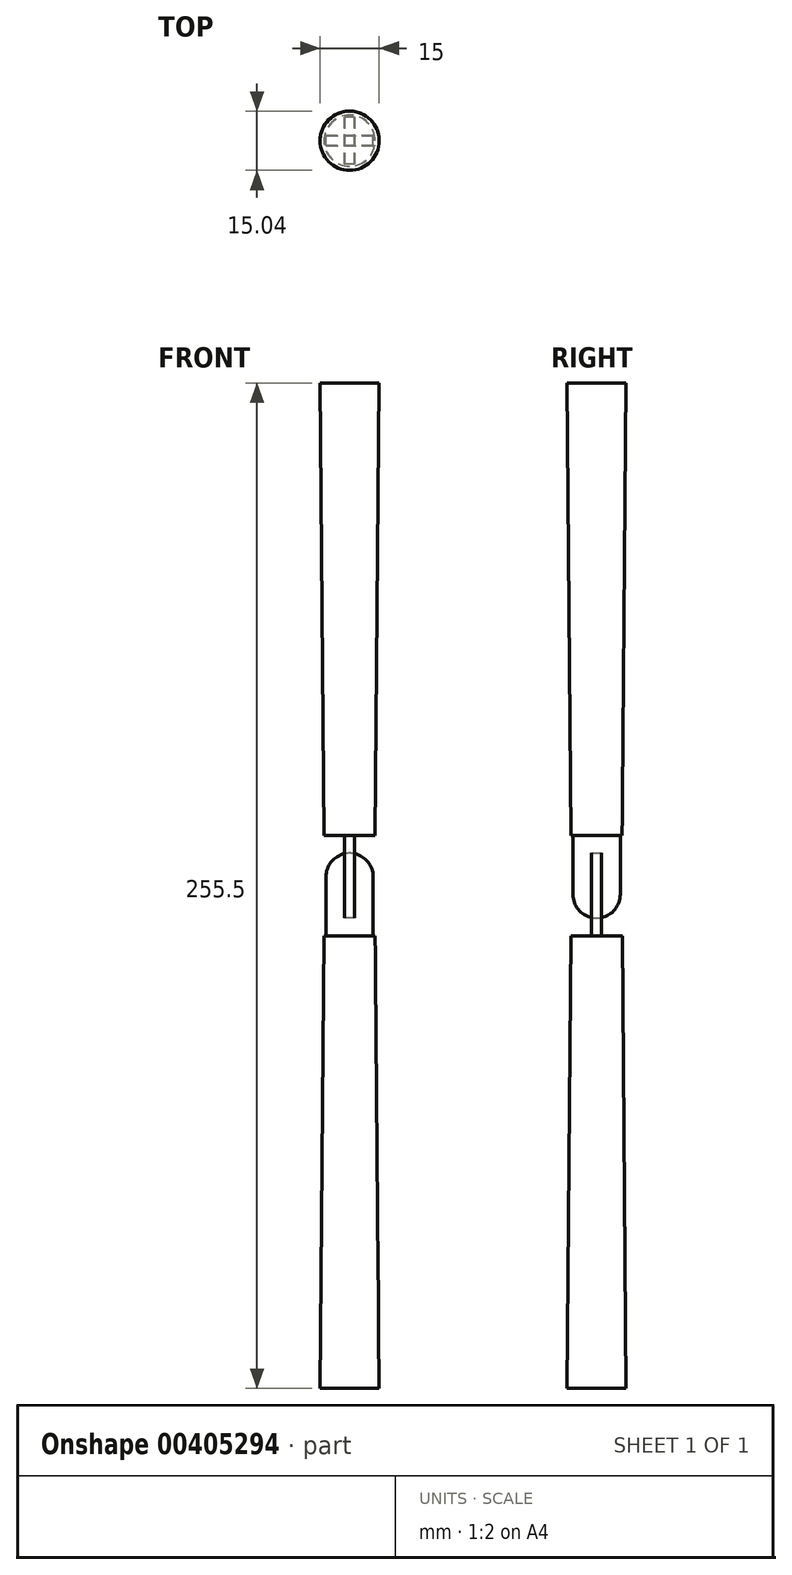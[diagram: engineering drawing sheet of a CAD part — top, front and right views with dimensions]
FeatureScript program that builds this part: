
annotation { "Feature Type Name" : "Feature", "Feature Type Description" : "" }
export const myFeature = defineFeature(function(context is Context, id is Id, definition is map)
    precondition{}
    {
        {
            var Q0;
            Q0=qCreatedBy(makeId("Front.planeOp"),FACE);
            var sketch = newSketch(context, id + "F0", { "sketchPlane" : qUnion([Q0])});
            skLineSegment(sketch, "E0.top", {"start": v(-6, 0) * mm, "end": v(6, 0) * mm});
            skLineSegment(sketch, "E0.left", {"start": v(-6, 15) * mm, "end": v(-6, 0) * mm});
            skArc(sketch, "E1", {"start": v(6, 15) * mm, "mid": v(0, 21) * mm, "end": v(-6, 15) * mm});
            skArc(sketch, "E2", {"start": v(3, 15) * mm, "mid": v(-2.12, 17.12) * mm, "end": v(0, 12) * mm});
            skCircle(sketch, "E3", {"center": v(0, 6) * mm, "radius": 2 * mm});
            skArc(sketch, "E4", {"start": v(6, 6) * mm, "mid": v(4.24, 10.24) * mm, "end": v(0, 12) * mm});
            skLineSegment(sketch, "E5", {"start": v(6, 0) * mm, "end": v(6, 6) * mm});
            skArc(sketch, "E6", {"start": v(3, 15) * mm, "mid": v(4.5, 13.5) * mm, "end": v(6, 15) * mm});
            skPoint(sketch, "E7.start.orphan", {"position": v(3, 15) * mm});
            skSolve(sketch);
        }
        {
            var Q0;
            Q0=makeQuery(id+"F0.imprint","IMPRINT",FACE,{"disambiguationData":[TD([[makeQuery(id+"F0.imprint","IMPRINT",EDGE,{"derivedFrom":sQuery(id+"F0.wireOp",EDGE,"E0.top")}),1.0]])]});
            extrude(context, id + "F1", {"entities" : qUnion([Q0]), "endBound" : BoundingType.SYMMETRIC, "depth" : 2.5 * mm});
        }
        {
            var Q0;
            Q0=qCreatedBy(makeId("Right.planeOp"),FACE);
            var sketch = newSketch(context, id + "F2", { "sketchPlane" : qUnion([Q0])});
            skLineSegment(sketch, "E8", {"start": v(0, 0) * mm, "end": v(0, -115) * mm});
            skLineSegment(sketch, "E9", {"start": v(0, 0) * mm, "end": v(-6.5, 0) * mm});
            skLineSegment(sketch, "E10", {"start": v(-6.5, 0) * mm, "end": v(-7.5, -115) * mm});
            skLineSegment(sketch, "E11", {"start": v(-7.5, -115) * mm, "end": v(0, -115) * mm});
            skSolve(sketch);
        }
        {
            var Q0;
            Q0=makeQuery(id+"F2.imprint","IMPRINT",FACE,{"disambiguationData":[TD([[makeQuery(id+"F2.imprint","IMPRINT",EDGE,{"derivedFrom":sQuery(id+"F2.wireOp",EDGE,"E8")}),-1.0]])]});
            var Q1;
            Q1=sQuery(id+"F2.wireOp",EDGE,"E8");
            revolve(context, id + "F3", {"operationType" : NewBodyOperationType.ADD, "entities" : qUnion([Q0]), "axis" : qUnion([Q1]), "revolveType" : RevolveType.FULL});
        }
        {
            var Q0;
            Q0=qCreatedBy(makeId("Front.planeOp"),FACE);
            var sketch = newSketch(context, id + "F4", { "sketchPlane" : qUnion([Q0])});
            skLineSegment(sketch, "E12.bottom", {"start": v(0, 0) * mm, "end": v(-6, 0) * mm});
            skLineSegment(sketch, "E12.top", {"start": v(0, 15) * mm, "end": v(-6, 15) * mm});
            skLineSegment(sketch, "E12.left", {"start": v(0, 0) * mm, "end": v(0, 15) * mm});
            skLineSegment(sketch, "E12.right", {"start": v(-6, 0) * mm, "end": v(-6, 15) * mm});
            skLineSegment(sketch, "E13.bottom", {"start": v(0, 0) * mm, "end": v(6, 0) * mm});
            skLineSegment(sketch, "E13.top", {"start": v(0, 15) * mm, "end": v(6, 15) * mm});
            skLineSegment(sketch, "E13.right", {"start": v(6, 0) * mm, "end": v(6, 15) * mm});
            skArc(sketch, "E14", {"start": v(-6, 15) * mm, "mid": v(0, 21) * mm, "end": v(6, 15) * mm});
            skLineSegment(sketch, "E15", {"start": v(0, 0) * mm, "end": v(-6.5, 0) * mm});
            skLineSegment(sketch, "E16", {"start": v(-6.5, 0) * mm, "end": v(-7.5, -115) * mm});
            skLineSegment(sketch, "E17", {"start": v(-7.5, -115) * mm, "end": v(0, -115) * mm});
            skLineSegment(sketch, "E18", {"start": v(0, -115) * mm, "end": v(0, 0) * mm});
            skSolve(sketch);
        }
        {
            var Q0;
            {var subQ0=sQuery(id+"F4.wireOp",EDGE,"E16");Q0=makeQuery(id+"F4.imprint","IMPRINT",FACE,{"disambiguationData":[TD([[makeQuery(id+"F4.imprint","IMPRINT",EDGE,{"derivedFrom":subQ0}),1.0]])]});}
            var Q1;
            Q1 = qSketchRegion(id + "F7", true);
            var Q2;
            Q2=sQuery(id+"F4.wireOp",EDGE,"E18");
            revolve(context, id + "F5", {"entities" : qUnion([Q0, Q1]), "axis" : qUnion([Q2]), "revolveType" : RevolveType.FULL});
        }
        {
            var Q0;
            Q0=makeQuery(id+"F4.imprint","IMPRINT",FACE,{"disambiguationData":[TD([[makeQuery(id+"F4.imprint","IMPRINT",EDGE,{"derivedFrom":sQuery(id+"F4.wireOp",EDGE,"E12.top")}),1.0]])]});
            var Q1;
            Q1=makeQuery(id+"F4.imprint","IMPRINT",FACE,{"disambiguationData":[TD([[makeQuery(id+"F4.imprint","IMPRINT",EDGE,{"derivedFrom":sQuery(id+"F4.wireOp",EDGE,"E13.bottom")}),1.0]])]});
            var Q2;
            Q2=makeQuery(id+"F4.imprint","IMPRINT",FACE,{"disambiguationData":[TD([[makeQuery(id+"F4.imprint","IMPRINT",EDGE,{"derivedFrom":sQuery(id+"F4.wireOp",EDGE,"E12.top")}),-1.0]])]});
            extrude(context, id + "F6", {"entities" : qUnion([Q0, Q1, Q2]), "operationType" : NewBodyOperationType.ADD, "endBound" : BoundingType.SYMMETRIC, "depth" : 2.5 * mm});
        }
        {
            var Q0;
            Q0=qCreatedBy(makeId("Right.planeOp"),FACE);
            var sketch = newSketch(context, id + "F7", { "sketchPlane" : qUnion([Q0])});
            skLineSegment(sketch, "E19.bottom", {"start": v(0, 25.5) * mm, "end": v(6, 25.5) * mm});
            skLineSegment(sketch, "E19.top", {"start": v(0, 10.5) * mm, "end": v(6, 10.5) * mm});
            skLineSegment(sketch, "E19.left", {"start": v(0, 25.5) * mm, "end": v(0, 10.5) * mm});
            skLineSegment(sketch, "E19.right", {"start": v(6, 25.5) * mm, "end": v(6, 10.5) * mm});
            skLineSegment(sketch, "E20.bottom", {"start": v(0, 25.5) * mm, "end": v(-6, 25.5) * mm});
            skLineSegment(sketch, "E20.top", {"start": v(0, 10.5) * mm, "end": v(-6, 10.5) * mm});
            skLineSegment(sketch, "E20.right", {"start": v(-6, 25.5) * mm, "end": v(-6, 10.5) * mm});
            skArc(sketch, "E21", {"start": v(6, 10.5) * mm, "mid": v(0, 4.5) * mm, "end": v(-6, 10.5) * mm});
            skPoint(sketch, "E22.endSnap0", {"position": v(0, 4.5) * mm});
            skLineSegment(sketch, "E23", {"start": v(0, 6) * mm, "end": v(0, 4.5) * mm});
            skLineSegment(sketch, "E24.MirrorCS", {"start": v(-7.54, 140.5) * mm, "end": v(-0.04, 140.5) * mm});
            skLineSegment(sketch, "E25.MirrorCS", {"start": v(-6.54, 25.5) * mm, "end": v(-7.54, 140.5) * mm});
            skLineSegment(sketch, "E26.MirrorCS", {"start": v(-0.04, 25.5) * mm, "end": v(-6.54, 25.5) * mm});
            skLineSegment(sketch, "E27.MirrorCS", {"start": v(-0.04, 25.5) * mm, "end": v(-0.04, 140.5) * mm});
            skSolve(sketch);
        }
        {
            var Q0;
            Q0=makeQuery(id+"F7.imprint","IMPRINT",FACE,{"disambiguationData":[TD([[makeQuery(id+"F7.imprint","IMPRINT",EDGE,{"derivedFrom":sQuery(id+"F7.wireOp",EDGE,"E24.MirrorCS")}),-1.0]])]});
            var Q1;
            Q1=sQuery(id+"F7.wireOp",EDGE,"E27.MirrorCS");
            revolve(context, id + "F8", {"entities" : qUnion([Q0]), "axis" : qUnion([Q1]), "revolveType" : RevolveType.FULL});
        }
        {
            var Q0;
            {var subQ1=sQuery(id+"F7.wireOp",EDGE,"E20.bottom");Q0=makeQuery(id+"F7.imprint","IMPRINT",FACE,{"disambiguationData":[TD([[makeQuery(id+"F7.imprint","IMPRINT",EDGE,{"derivedFrom":subQ1}),1.0]])]});}
            var Q1;
            Q1=makeQuery(id+"F7.imprint","IMPRINT",FACE,{"disambiguationData":[TD([[makeQuery(id+"F7.imprint","IMPRINT",EDGE,{"derivedFrom":sQuery(id+"F7.wireOp",EDGE,"E19.bottom")}),-1.0]])]});
            var Q2;
            {var subQ0=sQuery(id+"F7.wireOp",EDGE,"E19.top");Q2=makeQuery(id+"F7.imprint","IMPRINT",FACE,{"disambiguationData":[TD([[makeQuery(id+"F7.imprint","IMPRINT",EDGE,{"derivedFrom":subQ0}),-1.0]])]});}
            extrude(context, id + "F9", {"entities" : qUnion([Q0, Q1, Q2]), "endBound" : BoundingType.SYMMETRIC, "depth" : 2.5 * mm});
        }
    });
